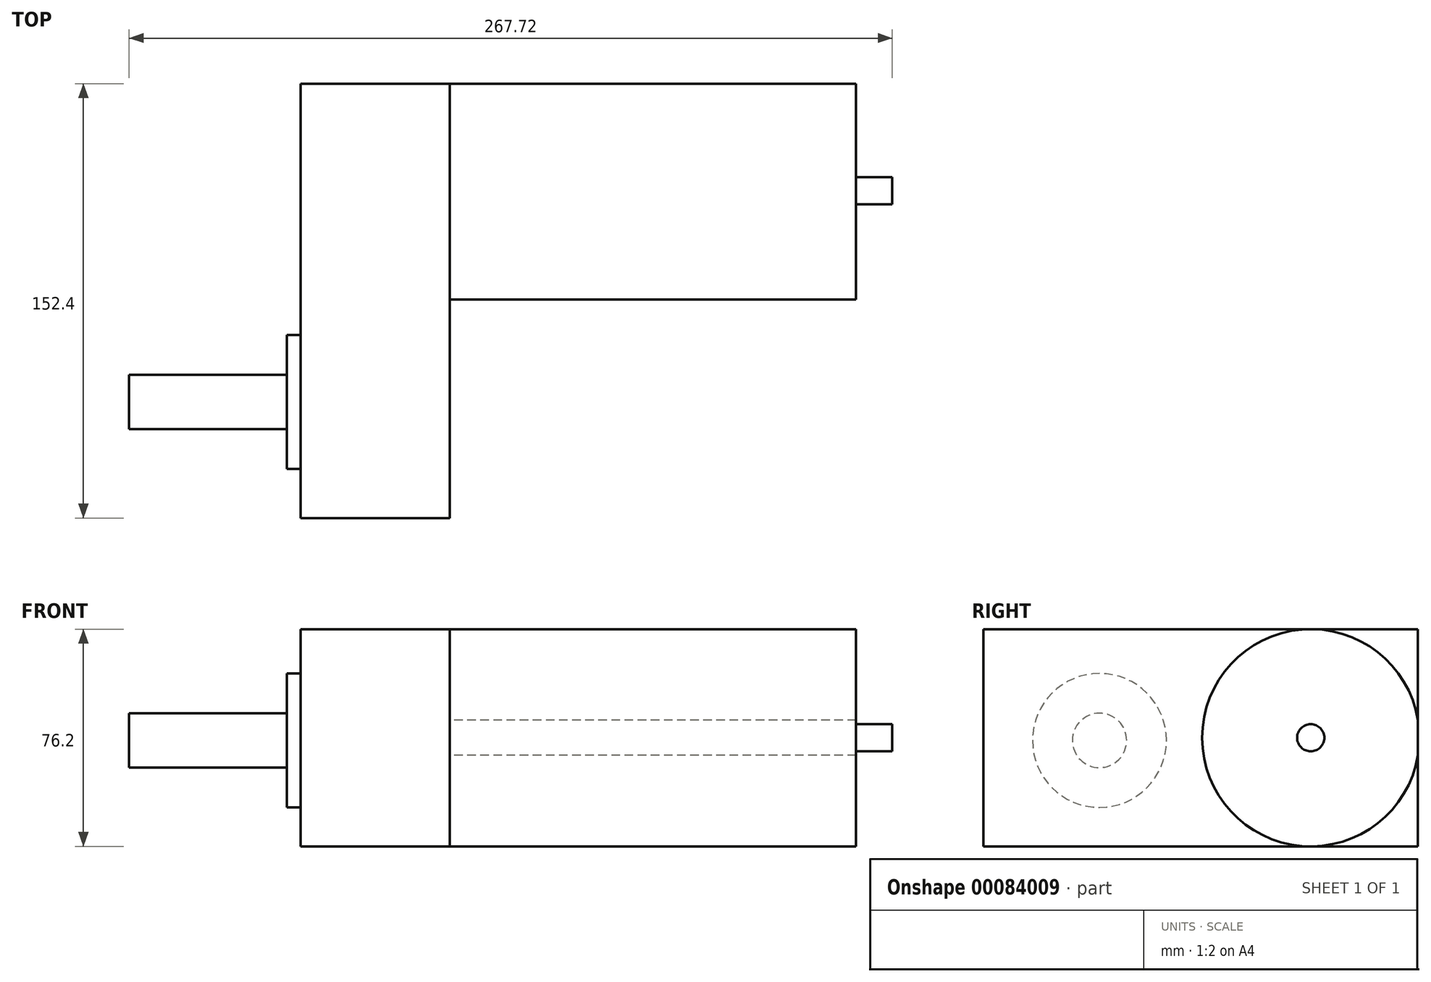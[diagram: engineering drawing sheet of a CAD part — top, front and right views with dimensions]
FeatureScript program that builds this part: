
annotation { "Feature Type Name" : "Feature", "Feature Type Description" : "" }
export const myFeature = defineFeature(function(context is Context, id is Id, definition is map)
    precondition{}
    {
        {
            var Q0;
            Q0=qCreatedBy(makeId("Top.planeOp"),FACE);
            var sketch = newSketch(context, id + "F0", { "sketchPlane" : qUnion([Q0])});
            skLineSegment(sketch, "E0.bottom", {"start": v(0, 0) * mm, "end": v(52.32, 0) * mm});
            skLineSegment(sketch, "E0.top", {"start": v(0, 152.4) * mm, "end": v(52.32, 152.4) * mm});
            skLineSegment(sketch, "E0.left", {"start": v(0, 0) * mm, "end": v(0, 152.4) * mm});
            skLineSegment(sketch, "E0.right", {"start": v(52.32, 0) * mm, "end": v(52.32, 152.4) * mm});
            skSolve(sketch);
        }
        {
            var Q0;
            Q0=makeQuery(id+"F0.imprint","IMPRINT",FACE,{"disambiguationData":[TD([[makeQuery(id+"F0.imprint","IMPRINT",EDGE,{"derivedFrom":sQuery(id+"F0.wireOp",EDGE,"E0.bottom")}),1.0]])]});
            extrude(context, id + "F1", {"entities" : qUnion([Q0]), "depth" : 76.2 * mm});
        }
        {
            var Q0;
            Q0=makeQuery(id+"F1.opExtrude","SWEPT_FACE",FACE,{"disambiguationData":[OSD([sQuery(id+"F0.wireOp",EDGE,"E0.right")])]});
            var sketch = newSketch(context, id + "F2", { "sketchPlane" : qUnion([Q0])});
            skCircle(sketch, "E1", {"center": v(114.8, 38.1) * mm, "radius": 38.1 * mm});
            skSolve(sketch);
        }
        {
            var Q0;
            {var subQ0=sQuery(id+"F2.wireOp",EDGE,"E1");var subQ1=sQuery(id+"F0.wireOp",EDGE,"E0.right");var subQ2=makeQuery(id+"F2.imprint","INTERSECT",VERTEX,{"derivedFrom":[makeQuery(id+"F1.opExtrude","CAP_EDGE",EDGE,{"disambiguationData":[OSD([subQ1])],"isStart":false}),subQ0]});Q0=makeQuery(id+"F2.imprint","IMPRINT",FACE,{"disambiguationData":[TD([[makeQuery(id+"F2.imprint","IMPRINT",EDGE,{"disambiguationData":[TD([[subQ2,-1.0]])],"derivedFrom":subQ0}),1.0]])]});}
            extrude(context, id + "F3", {"entities" : qUnion([Q0]), "operationType" : NewBodyOperationType.ADD, "depth" : 142.5 * mm});
        }
        {
            var Q0;
            Q0=makeQuery(id+"F1.opExtrude","SWEPT_FACE",FACE,{"disambiguationData":[OSD([sQuery(id+"F0.wireOp",EDGE,"E0.left")])]});
            var sketch = newSketch(context, id + "F4", { "sketchPlane" : qUnion([Q0])});
            skCircle(sketch, "E2", {"center": v(-40.7, 37.15) * mm, "radius": 23.5 * mm});
            skSolve(sketch);
        }
        {
            var Q0;
            Q0=makeQuery(id+"F4.imprint","IMPRINT",FACE,{"disambiguationData":[TD([[makeQuery(id+"F4.imprint","IMPRINT",EDGE,{"derivedFrom":sQuery(id+"F4.wireOp",EDGE,"E2")}),1.0]])]});
            extrude(context, id + "F5", {"entities" : qUnion([Q0]), "operationType" : NewBodyOperationType.ADD, "depth" : 4.83 * mm});
        }
        {
            var Q0;
            Q0=makeQuery(id+"F5.opExtrude","CAP_FACE",FACE,{"disambiguationData":[OSD([sQuery(id+"F4.wireOp",EDGE,"E2")])],"isStart":false});
            var sketch = newSketch(context, id + "F6", { "sketchPlane" : qUnion([Q0])});
            skCircle(sketch, "E3", {"center": v(-40.7, 37.15) * mm, "radius": 9.53 * mm});
            skSolve(sketch);
        }
        {
            var Q0;
            Q0=makeQuery(id+"F6.imprint","IMPRINT",FACE,{"disambiguationData":[TD([[makeQuery(id+"F6.imprint","IMPRINT",EDGE,{"derivedFrom":sQuery(id+"F6.wireOp",EDGE,"E3")}),1.0]])]});
            extrude(context, id + "F7", {"entities" : qUnion([Q0]), "operationType" : NewBodyOperationType.ADD, "depth" : 55.37 * mm});
        }
        {
            var Q0;
            Q0=makeQuery(id+"F3.opExtrude","CAP_FACE",FACE,{"disambiguationData":[OSD([sQuery(id+"F0.wireOp",EDGE,"E0.top"),sQuery(id+"F0.wireOp",EDGE,"E0.right"),sQuery(id+"F2.wireOp",EDGE,"E1")])],"isStart":false});
            var sketch = newSketch(context, id + "F8", { "sketchPlane" : qUnion([Q0])});
            skCircle(sketch, "E4", {"center": v(114.8, 38.1) * mm, "radius": 4.76 * mm});
            skSolve(sketch);
        }
        {
            var Q0;
            Q0=makeQuery(id+"F8.imprint","IMPRINT",FACE,{"disambiguationData":[TD([[makeQuery(id+"F8.imprint","IMPRINT",EDGE,{"derivedFrom":sQuery(id+"F8.wireOp",EDGE,"E4")}),1.0]])]});
            extrude(context, id + "F9", {"entities" : qUnion([Q0]), "operationType" : NewBodyOperationType.ADD, "depth" : 12.7 * mm});
        }
    });
